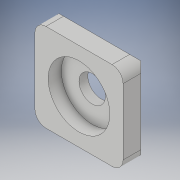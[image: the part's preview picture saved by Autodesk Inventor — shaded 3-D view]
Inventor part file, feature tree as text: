
AUTODESK INVENTOR PART (.ipt)
format: ipt  version: 2017 SP1 (Build 210196100, 196)  size: 128,512 bytes
history: native  units: in
note: dims shown in document units (in); Inventor stores cm internally (conversion verified against a paired STEP export)
features: sketch x2, extrude x1, hole x1, chamfer x1, fillet x1
ambient origin geometry x8: Origin, YZ Plane, XZ Plane, XY Plane, X Axis, Y Axis, Z Axis, Center Point
bodies: Solid1 (feature_tree)
feature tree (6):
  extrude  "Extrusion1"  Depth=0.25in TaperAngle=0.0deg
  hole  "Hole1"  [1 undecoded]
  chamfer  "Chamfer1"  Distance=0.125in
  fillet  "Fillet1"  [1 undecoded]
  sketch  "Sketch1"  dims[d0=1.0in d2=0.25in d3=0.0in]
  sketch  "Sketch2"  dims[d4=0.3in d5=0.75in d6=0.7in d7=0.15in d8=0.5635in d9=1.0in d10=0.8108in d11=0.05in d12=0.125in d13=45.0deg d14=0.125in]
note: 2 required parameter values undecoded (feature->parameter linkage not recoverable at this tier; creation-order binding heuristic only, values carry confidence <= 0.55)
